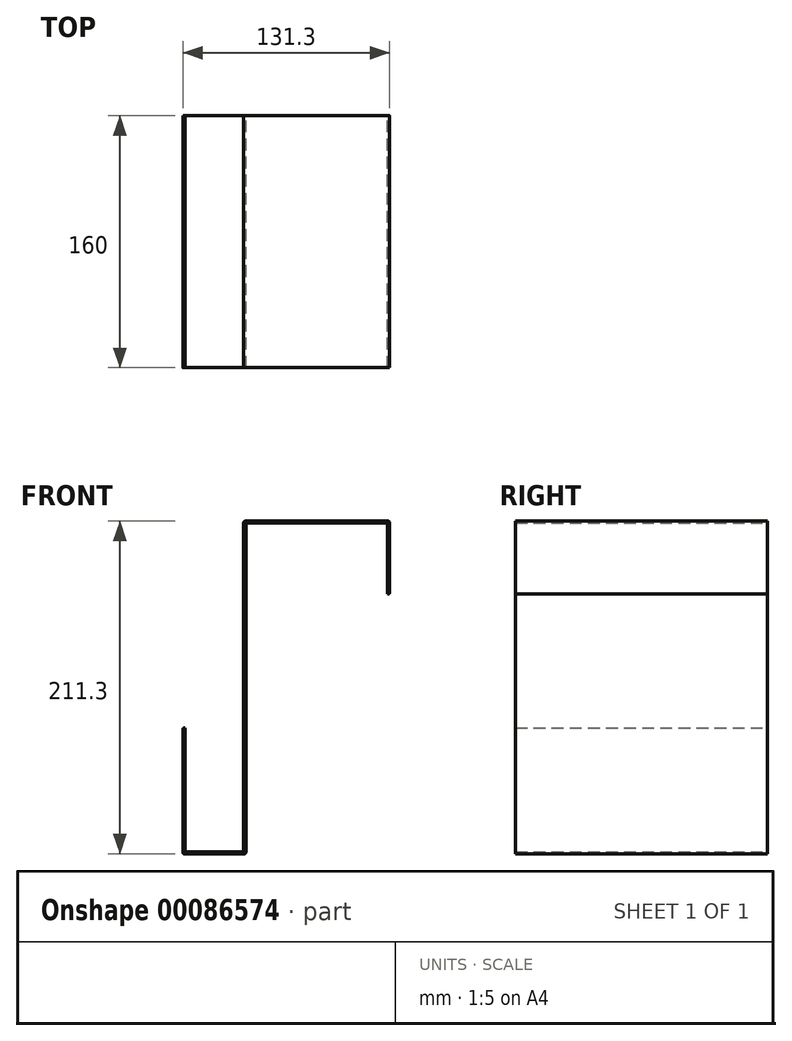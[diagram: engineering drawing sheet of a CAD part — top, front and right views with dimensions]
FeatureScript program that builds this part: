
annotation { "Feature Type Name" : "Feature", "Feature Type Description" : "" }
export const myFeature = defineFeature(function(context is Context, id is Id, definition is map)
    precondition{}
    {
        {
            var Q0;
            Q0=qCreatedBy(makeId("Front.planeOp"),FACE);
            var sketch = newSketch(context, id + "F0", { "sketchPlane" : qUnion([Q0])});
            skLineSegment(sketch, "E0", {"start": v(-157.25, -85) * mm, "end": v(-157.25, -165) * mm});
            skLineSegment(sketch, "E1", {"start": v(-157.25, -165) * mm, "end": v(-117.25, -165) * mm});
            skLineSegment(sketch, "E2", {"start": v(-117.25, -165) * mm, "end": v(-117.25, 45) * mm});
            skLineSegment(sketch, "E3", {"start": v(-117.25, 45) * mm, "end": v(-27.25, 45) * mm});
            skLineSegment(sketch, "E4", {"start": v(-27.25, 45) * mm, "end": v(-27.25, 0) * mm});
            skLineSegment(sketch, "E5.0", {"start": v(-25.95, 46.3) * mm, "end": v(-25.95, 0) * mm});
            skLineSegment(sketch, "E5.1", {"start": v(-155.95, -85) * mm, "end": v(-155.95, -163.7) * mm});
            skLineSegment(sketch, "E5.2", {"start": v(-155.95, -163.7) * mm, "end": v(-118.55, -163.7) * mm});
            skLineSegment(sketch, "E5.3", {"start": v(-118.55, -163.7) * mm, "end": v(-118.55, 46.3) * mm});
            skLineSegment(sketch, "E5.4", {"start": v(-118.55, 46.3) * mm, "end": v(-25.95, 46.3) * mm});
            skLineSegment(sketch, "E6", {"start": v(-27.25, 0) * mm, "end": v(-25.95, 0) * mm});
            skLineSegment(sketch, "E7", {"start": v(-155.95, -85) * mm, "end": v(-157.25, -85) * mm});
            skSolve(sketch);
        }
        {
            var Q0;
            Q0 = qSketchRegion(id + "F0", true);
            extrude(context, id + "F1", {"entities" : qUnion([Q0]), "endBound" : BoundingType.SYMMETRIC, "depth" : 160 * mm});
        }
        {
            var Q0;
            Q0=makeQuery(id+"F1.opExtrude","SWEPT_EDGE",EDGE,{"disambiguationData":[OSD([sQuery(id+"F0.wireOp",EDGE,"E5.3"),sQuery(id+"F0.wireOp",EDGE,"E5.4")])]});
            var Q1;
            Q1=makeQuery(id+"F1.opExtrude","SWEPT_EDGE",EDGE,{"disambiguationData":[OSD([sQuery(id+"F0.wireOp",EDGE,"E5.0"),sQuery(id+"F0.wireOp",EDGE,"E5.4")])]});
            var Q2;
            Q2=makeQuery(id+"F1.opExtrude","SWEPT_EDGE",EDGE,{"disambiguationData":[OSD([sQuery(id+"F0.wireOp",EDGE,"E1"),sQuery(id+"F0.wireOp",EDGE,"E2")])]});
            var Q3;
            Q3=makeQuery(id+"F1.opExtrude","SWEPT_EDGE",EDGE,{"disambiguationData":[OSD([sQuery(id+"F0.wireOp",EDGE,"E0"),sQuery(id+"F0.wireOp",EDGE,"E1")])]});
            var Q4;
            Q4=makeQuery(id+"F1.opExtrude","SWEPT_EDGE",EDGE,{"disambiguationData":[OSD([sQuery(id+"F0.wireOp",EDGE,"E5.0"),sQuery(id+"F0.wireOp",EDGE,"E6")])]});
            var Q5;
            Q5=makeQuery(id+"F1.opExtrude","SWEPT_EDGE",EDGE,{"disambiguationData":[OSD([sQuery(id+"F0.wireOp",EDGE,"E0"),sQuery(id+"F0.wireOp",EDGE,"E7")])]});
            var Q6;
            Q6=makeQuery(id+"F1.opExtrude","SWEPT_EDGE",EDGE,{"disambiguationData":[OSD([sQuery(id+"F0.wireOp",EDGE,"E5.1"),sQuery(id+"F0.wireOp",EDGE,"E5.2")])]});
            var Q7;
            Q7=makeQuery(id+"F1.opExtrude","SWEPT_EDGE",EDGE,{"disambiguationData":[OSD([sQuery(id+"F0.wireOp",EDGE,"E5.2"),sQuery(id+"F0.wireOp",EDGE,"E5.3")])]});
            fillet(context, id + "F2", {"entities" : qUnion([Q0, Q1, Q2, Q3, Q4, Q5, Q6, Q7]), "radius" : 1 * mm, "tangentPropagation" : true, "allowEdgeOverflow" : false});
        }
    });
